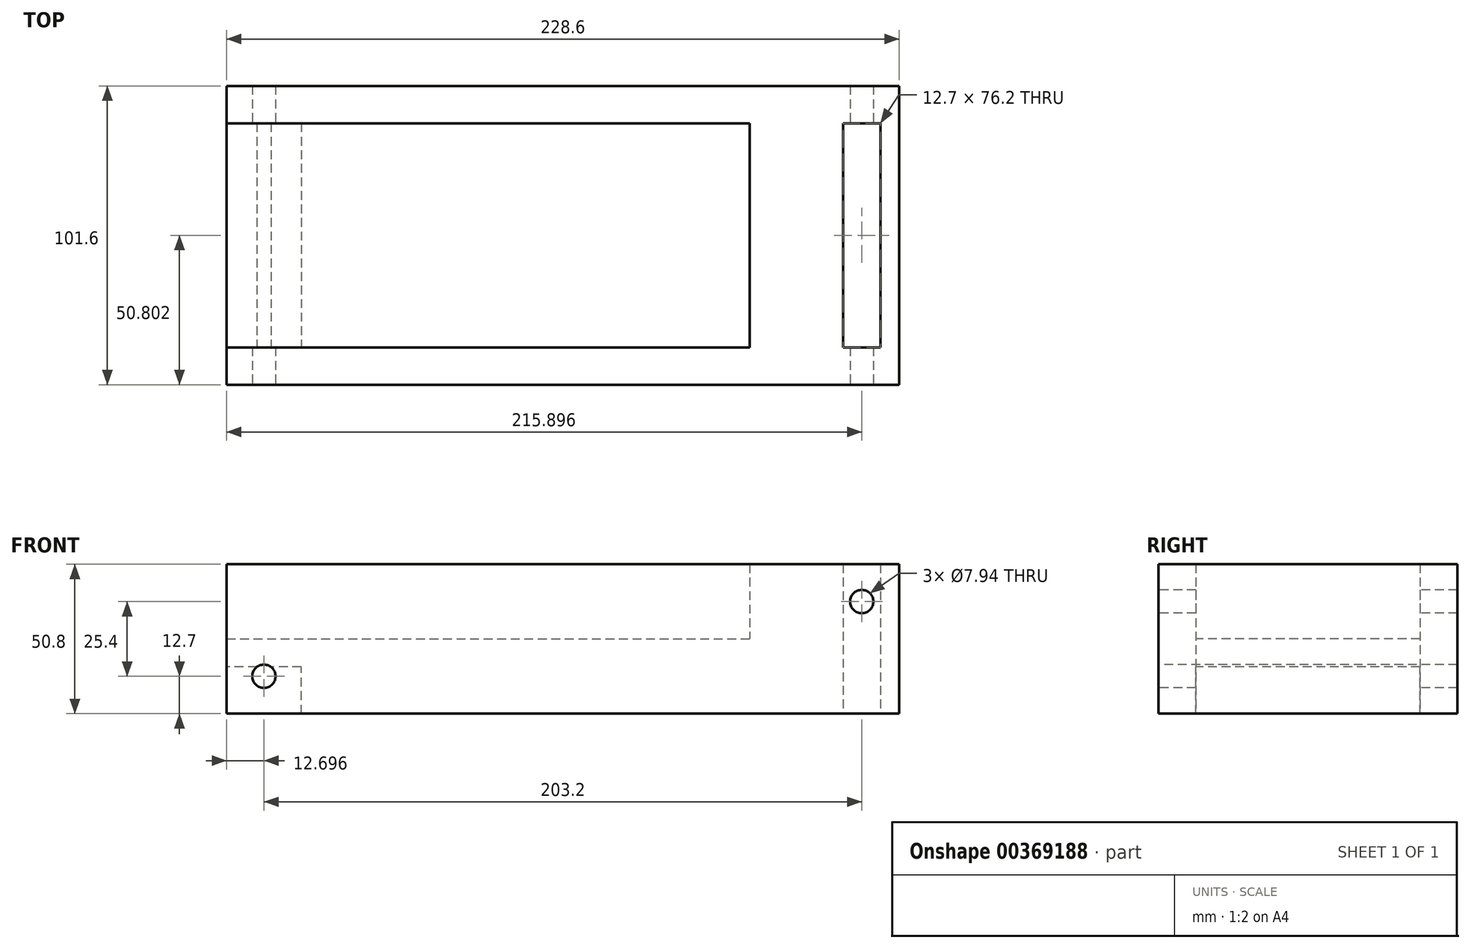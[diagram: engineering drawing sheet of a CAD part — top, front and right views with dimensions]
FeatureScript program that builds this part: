
annotation { "Feature Type Name" : "Feature", "Feature Type Description" : "" }
export const myFeature = defineFeature(function(context is Context, id is Id, definition is map)
    precondition{}
    {
        {
            var Q0;
            Q0=qCreatedBy(makeId("Top.planeOp"),FACE);
            var sketch = newSketch(context, id + "F0", { "sketchPlane" : qUnion([Q0])});
            skLineSegment(sketch, "E0.bottom", {"start": v(-74.58, 53.35) * mm, "end": v(154.02, 53.35) * mm});
            skLineSegment(sketch, "E0.top", {"start": v(-74.58, -48.25) * mm, "end": v(154.02, -48.25) * mm});
            skLineSegment(sketch, "E0.left", {"start": v(-74.58, 53.35) * mm, "end": v(-74.58, -48.25) * mm});
            skLineSegment(sketch, "E0.right", {"start": v(154.02, 53.35) * mm, "end": v(154.02, -48.25) * mm});
            skLineSegment(sketch, "E1.bottom", {"start": v(134.97, 40.65) * mm, "end": v(147.67, 40.65) * mm});
            skLineSegment(sketch, "E1.top", {"start": v(134.97, -35.55) * mm, "end": v(147.67, -35.55) * mm});
            skLineSegment(sketch, "E1.left", {"start": v(134.97, 40.65) * mm, "end": v(134.97, -35.55) * mm});
            skLineSegment(sketch, "E1.right", {"start": v(147.67, 40.65) * mm, "end": v(147.67, -35.55) * mm});
            skLineSegment(sketch, "E2.bottom", {"start": v(-74.58, 40.65) * mm, "end": v(103.22, 40.65) * mm});
            skLineSegment(sketch, "E2.top", {"start": v(-74.58, -35.55) * mm, "end": v(103.22, -35.55) * mm});
            skLineSegment(sketch, "E2.left", {"start": v(-74.58, 40.65) * mm, "end": v(-74.58, -35.55) * mm});
            skLineSegment(sketch, "E2.right", {"start": v(103.22, 40.65) * mm, "end": v(103.22, -35.55) * mm});
            skSolve(sketch);
        }
        {
            var Q0;
            {var subQ1=sQuery(id+"F0.wireOp",EDGE,"E0.bottom");Q0=makeQuery(id+"F0.imprint","IMPRINT",FACE,{"disambiguationData":[TD([[makeQuery(id+"F0.imprint","IMPRINT",EDGE,{"derivedFrom":subQ1}),-1.0]])]});}
            extrude(context, id + "F1", {"entities" : qUnion([Q0]), "depth" : 50.8 * mm, "symmetric" : true});
        }
        {
            var Q0;
            Q0=makeQuery(id+"F0.imprint","IMPRINT",FACE,{"disambiguationData":[TD([[makeQuery(id+"F0.imprint","IMPRINT",EDGE,{"derivedFrom":sQuery(id+"F0.wireOp",EDGE,"E2.bottom")}),-1.0]])]});
            extrude(context, id + "F2", {"entities" : qUnion([Q0]), "operationType" : NewBodyOperationType.ADD, "oppositeDirection" : true, "depth" : 25.4 * mm});
        }
        {
            var Q0;
            Q0=makeQuery(id+"F1.opExtrude","SWEPT_FACE",FACE,{"disambiguationData":[OSD([sQuery(id+"F0.wireOp",EDGE,"E0.top")])]});
            var sketch = newSketch(context, id + "F3", { "sketchPlane" : qUnion([Q0])});
            skCircle(sketch, "E3", {"center": v(141.32, 12.7) * mm, "radius": 3.97 * mm});
            skSolve(sketch);
        }
        {
            var Q0;
            Q0 = qSketchRegion(id + "F3", true);
            extrude(context, id + "F4", {"entities" : qUnion([Q0]), "operationType" : NewBodyOperationType.REMOVE, "oppositeDirection" : true, "depth" : 254 * mm});
        }
        {
            var Q0;
            Q0=makeQuery(id+"F1.opExtrude","SWEPT_FACE",FACE,{"disambiguationData":[OSD([sQuery(id+"F0.wireOp",EDGE,"E0.top")])]});
            var sketch = newSketch(context, id + "F5", { "sketchPlane" : qUnion([Q0])});
            skCircle(sketch, "E4", {"center": v(-61.88, -12.7) * mm, "radius": 3.97 * mm});
            skSolve(sketch);
        }
        {
            var Q0;
            Q0 = qSketchRegion(id + "F5", true);
            extrude(context, id + "F6", {"entities" : qUnion([Q0]), "operationType" : NewBodyOperationType.REMOVE, "oppositeDirection" : true, "depth" : 152.4 * mm});
        }
        {
            var Q0;
            {var subQ0=sQuery(id+"F0.wireOp",EDGE,"E2.left");var subQ1=sQuery(id+"F0.wireOp",EDGE,"E0.left");Q0=makeQuery(id+"F2.boolean.opBoolean","MERGE",FACE,{"derivedFrom":[makeQuery(id+"F1.opExtrude","SWEPT_FACE",FACE,{"disambiguationData":[OSD([subQ1]),TDD([makeQuery(id+"F0.imprint","IMPRINT",EDGE,{"disambiguationData":[TD([[makeQuery(id+"F0.imprint","INTERSECT",VERTEX,{"derivedFrom":[sQuery(id+"F0.wireOp",EDGE,"E0.bottom"),subQ1]}),-1.0]])],"derivedFrom":subQ1})])]}),makeQuery(id+"F1.opExtrude","SWEPT_FACE",FACE,{"disambiguationData":[OSD([subQ1]),TDD([makeQuery(id+"F0.imprint","IMPRINT",EDGE,{"disambiguationData":[TD([[makeQuery(id+"F0.imprint","INTERSECT",VERTEX,{"derivedFrom":[sQuery(id+"F0.wireOp",EDGE,"E0.top"),subQ1]}),1.0]])],"derivedFrom":subQ1})])]}),makeQuery(id+"F2.opExtrude","SWEPT_FACE",FACE,{"disambiguationData":[OSD([subQ0])]})]});}
            var sketch = newSketch(context, id + "F7", { "sketchPlane" : qUnion([Q0])});
            skLineSegment(sketch, "E5.bottom", {"start": v(-40.65, -25.4) * mm, "end": v(35.55, -25.4) * mm});
            skLineSegment(sketch, "E5.top", {"start": v(-40.65, -9.53) * mm, "end": v(35.55, -9.52) * mm});
            skLineSegment(sketch, "E5.left", {"start": v(-40.65, -25.4) * mm, "end": v(-40.65, -9.53) * mm});
            skLineSegment(sketch, "E5.right", {"start": v(35.55, -25.4) * mm, "end": v(35.55, -9.52) * mm});
            skSolve(sketch);
        }
        {
            var Q0;
            Q0 = qSketchRegion(id + "F7", true);
            extrude(context, id + "F8", {"entities" : qUnion([Q0]), "operationType" : NewBodyOperationType.REMOVE, "oppositeDirection" : true, "depth" : 25.4 * mm, "offsetDistance" : 25.4 * mm});
        }
    });
